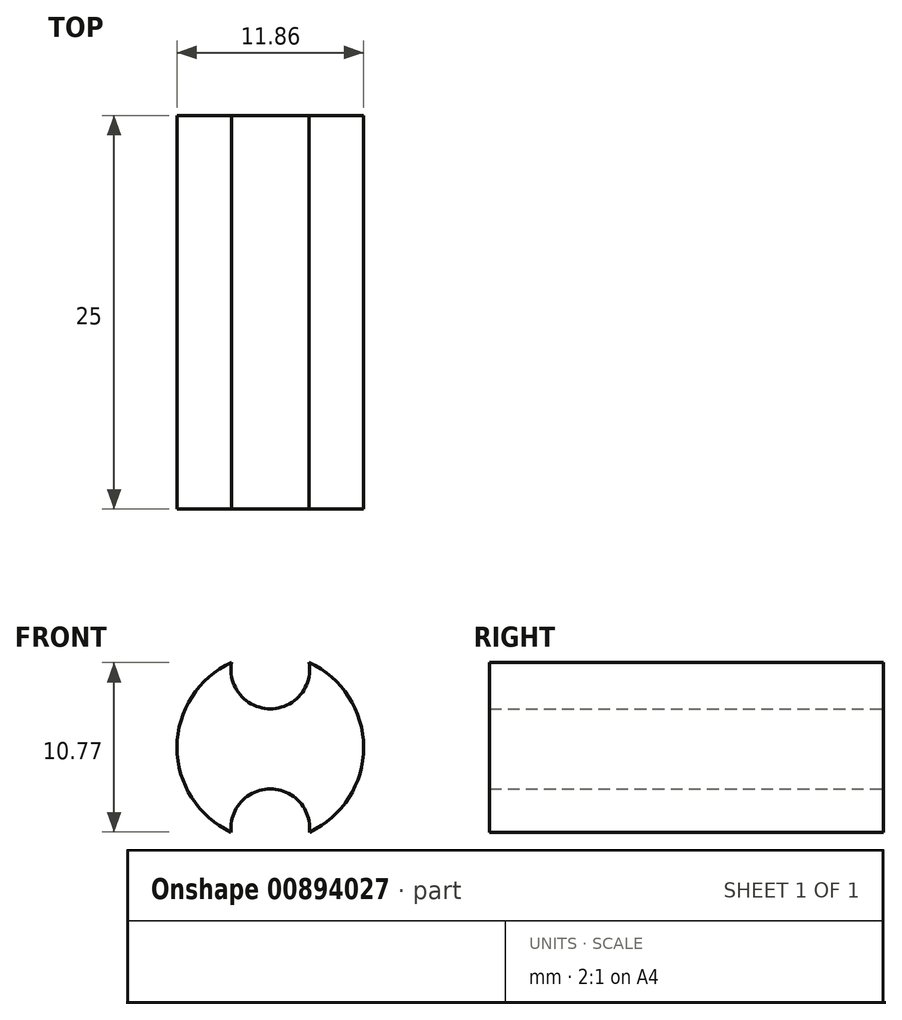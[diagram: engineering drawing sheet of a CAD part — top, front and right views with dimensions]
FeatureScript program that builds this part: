
annotation { "Feature Type Name" : "Feature", "Feature Type Description" : "" }
export const myFeature = defineFeature(function(context is Context, id is Id, definition is map)
    precondition{}
    {
        {
            var Q0;
            Q0=qCreatedBy(makeId("Front.planeOp"),FACE);
            var sketch = newSketch(context, id + "F0", { "sketchPlane" : qUnion([Q0])});
            skCircle(sketch, "E0", {"center": v(-62.68, 5.14) * mm, "radius": 5.93 * mm});
            skSolve(sketch);
        }
        {
            var Q0;
            Q0=makeQuery(id+"F0.imprint","IMPRINT",FACE,{"disambiguationData":[TD([[makeQuery(id+"F0.imprint","IMPRINT",EDGE,{"derivedFrom":sQuery(id+"F0.wireOp",EDGE,"E0")}),1.0]])]});
            extrude(context, id + "F1", {"entities" : qUnion([Q0]), "depth" : 25 * mm, "offsetDistance" : 25 * mm});
        }
        {
            var Q0;
            Q0=makeQuery(id+"F1.opExtrude","CAP_FACE",FACE,{"disambiguationData":[OSD([sQuery(id+"F0.wireOp",EDGE,"E0")])],"isStart":true});
            var sketch = newSketch(context, id + "F2", { "sketchPlane" : qUnion([Q0])});
            skLineSegment(sketch, "E1", {"start": v(62.68, 5.14) * mm, "end": v(62.68, 0) * mm});
            skLineSegment(sketch, "E2", {"start": v(62.68, 0) * mm, "end": v(62.68, 10.1) * mm, "construction": true});
            skSolve(sketch);
        }
        {
            var Q0;
            Q0=sQuery(id+"F2.wireOp",VERTEX,"E1.end");
            var Q1;
            Q1=sQuery(id+"F2.wireOp",VERTEX,"E2.end");
            var Q2;
            Q2=makeQuery(id+"F1.opExtrude","SWEPT_BODY",BODY,{"disambiguationData":[OSD([sQuery(id+"F0.wireOp",EDGE,"E0")])]});
            hole(context, id + "F3", {"style" : HoleStyle.SIMPLE, "endStyle" : HoleEndStyle.BLIND, "holeDiameter" : 5 * mm, "majorDiameter" : 5 * mm, "holeDepth" : 30 * mm, "isTappedThrough" : true, "tappedDepth" : 12 * mm, "tapClearance" : 3, "locations" : qUnion([Q0, Q1]), "scope" : qUnion([Q2])});
        }
    });
